# Revit family: Haworth_Very_ChairStool_SledWireFrame_EU_PRELIMINARY
name_source: partatom
category: Furniture
revit_build: Autodesk Revit 2018 (Build: 20170223_1515(x64)
units: mm (PartAtom-declared; Revit-internal decimal feet)

## family parameters
Always vertical = Yes
Cut with Voids When Loaded = No
OmniClass Number = 23.40.70.14.64.21
OmniClass Title = Systems Furniture
Room Calculation Point = No
Shared = No
Work Plane-Based = No

## types (6) — shared parameters
Actual Depth = 59 cm
Actual Width = 55 cm
Arm Cap Finish = Haworth _ Polymer _ Slate
Assembly Code = E2020200
Description = Haworth - Very - Seminar - Visitor - Sled Wire Frame
Manufacturer = Haworth
Model = 62X0
Rack Finish = Haworth _ Polymer _ Undecided
Revision Number = 6
Size = Verify Final Dim. w/ Haworth
Sustainability Info = https://www.haworth.com
Tablet Finish = Haworth _ Laminate _ Linen H-WL
URL = https://www.haworth.com
URL - Product = https://www.haworth.com
Warranty = http://www.haworth.com
With Back Cushion = Yes
With Seat Cushion = Yes

## per-type parameters (varying)
| type | Actual Height | Chair | Stool | Tablet | With Arms |
| Stool with Arms | 106 cm | No | Yes | No | Yes |
| Chair with Arms | 78 cm | Yes | No | No | Yes |
| Stool without Arms | 106 cm | No | Yes | No | No |
| Chair without Arms | 78 cm | Yes | No | No | No |
| Chair with Tablet | 78 cm | Yes | No | Yes | No |
| Stool with Tablet | 106 cm | No | Yes | Yes | No |

## geometry (parser evidence)
native form markers: Blend x2, Sweep x15
no freeform markers — native parametric forms only
